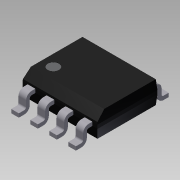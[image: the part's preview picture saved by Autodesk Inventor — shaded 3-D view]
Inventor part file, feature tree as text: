
AUTODESK INVENTOR PART (.ipt)
format: ipt  version: 2011 (Build 150239000, 239)  size: 283,648 bytes
history: native  units: mm
features: projected_geometry x6, extrude x5, sketch x5, other x3, mirror x1, pattern_linear x1
ambient origin geometry x8: Origin, YZ Plane, XZ Plane, XY Plane, X Axis, Y Axis, Z Axis, Center Point
feature tree (21):
  other  "Твердое тело1"
  extrude  "Выдавливание1"  Depth=2.5mm
  extrude  "Выдавливание4"  Depth=2.0mm
  extrude  "Выдавливание5"  Depth=5.0mm
  other  "РабПлоскость1"
  extrude  "Выдавливание6"  Depth=4.0mm
  other  "РабПлоскость2"
  mirror  "Зеркальное отражение1"
  pattern_linear  "Прямоуг.массив1"  Spacing1=1.75mm  [1 undecoded]
  extrude  "Выдавливание7"  Depth=0.625mm
  sketch  "Эскиз1"
  sketch  "Эскиз4"
  sketch  "Эскиз5"
  projected_geometry  "Спроецированная петля3"
  projected_geometry  "Спроецированная петля4"
  projected_geometry  "Спроецированная петля5"
  sketch  "Эскиз6"
  projected_geometry  "Спроецированная петля6"
  projected_geometry  "Спроецированная петля7"
  projected_geometry  "Спроецированная петля8"
  sketch  "Эскиз7"
note: 1 required parameter value undecoded (feature->parameter linkage not recoverable at this tier; creation-order binding heuristic only, values carry confidence <= 0.55)
